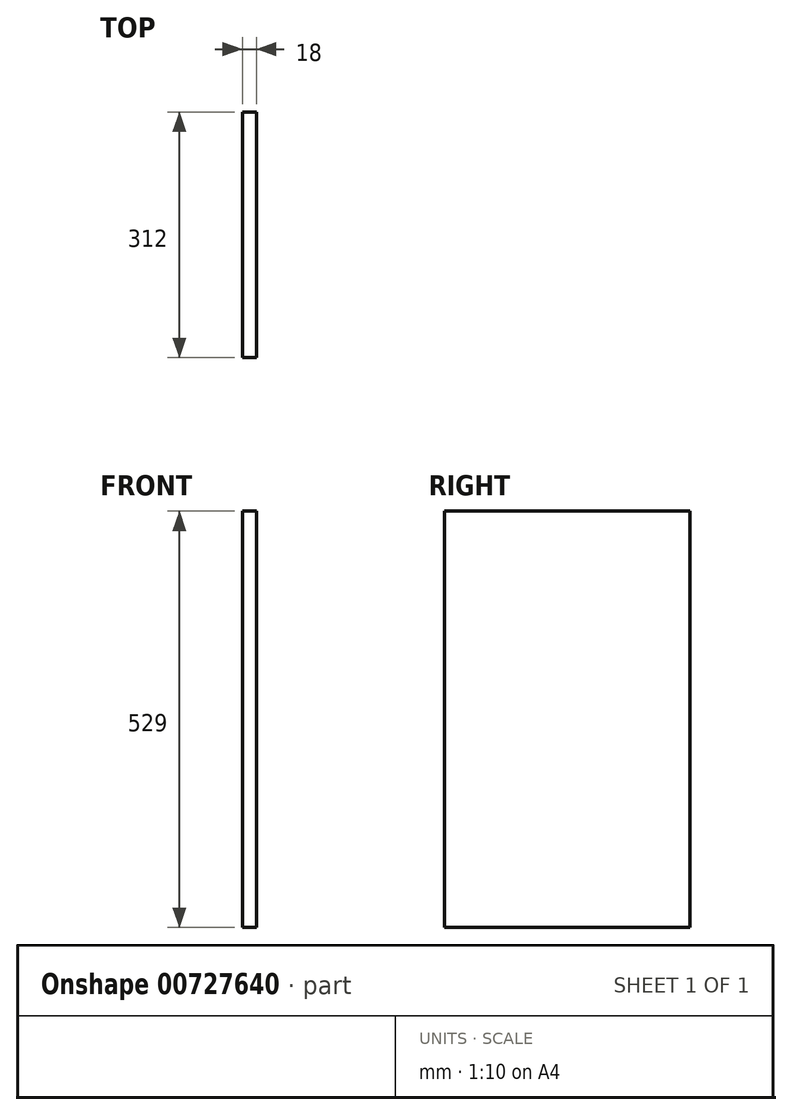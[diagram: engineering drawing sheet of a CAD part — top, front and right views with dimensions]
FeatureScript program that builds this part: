
annotation { "Feature Type Name" : "Feature", "Feature Type Description" : "" }
export const myFeature = defineFeature(function(context is Context, id is Id, definition is map)
    precondition{}
    {
        {
            var Q0;
            Q0=qCreatedBy(makeId("Right.planeOp"),FACE);
            var sketch = newSketch(context, id + "F0", { "sketchPlane" : qUnion([Q0])});
            skLineSegment(sketch, "E0.bottom", {"start": v(-156, 264.5) * mm, "end": v(156, 264.5) * mm});
            skLineSegment(sketch, "E0.top", {"start": v(-156, -264.5) * mm, "end": v(156, -264.5) * mm});
            skLineSegment(sketch, "E0.left", {"start": v(-156, 264.5) * mm, "end": v(-156, -264.5) * mm});
            skLineSegment(sketch, "E0.right", {"start": v(156, 264.5) * mm, "end": v(156, -264.5) * mm});
            skLineSegment(sketch, "E1", {"start": v(-156, 264.5) * mm, "end": v(156, -264.5) * mm, "construction": true});
            skSolve(sketch);
        }
        {
            var Q0;
            Q0 = qSketchRegion(id + "F0", true);
            extrude(context, id + "F1", {"entities" : qUnion([Q0]), "depth" : 18 * mm, "offsetDistance" : 25 * mm});
        }
    });
